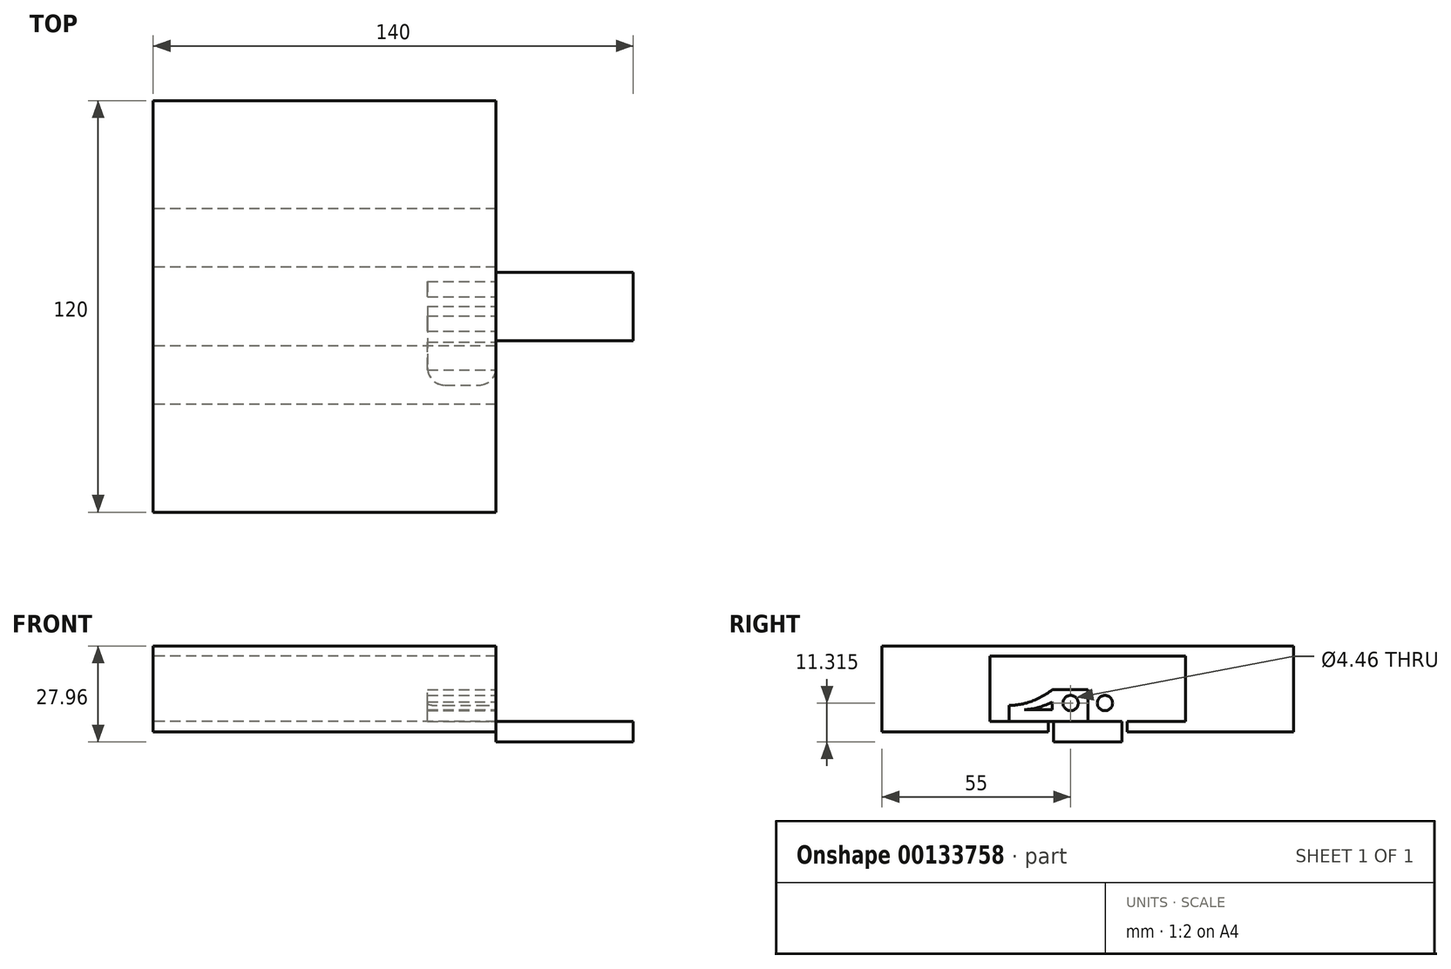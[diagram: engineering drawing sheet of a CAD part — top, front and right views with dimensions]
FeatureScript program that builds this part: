
annotation { "Feature Type Name" : "Feature", "Feature Type Description" : "" }
export const myFeature = defineFeature(function(context is Context, id is Id, definition is map)
    precondition{}
    {
        {
            var Q0;
            Q0=qCreatedBy(makeId("Right.planeOp"),FACE);
            var sketch = newSketch(context, id + "F0", { "sketchPlane" : qUnion([Q0])});
            skLineSegment(sketch, "E0", {"start": v(0, 0) * mm, "end": v(48.5, 0) * mm});
            skLineSegment(sketch, "E1", {"start": v(48.5, 0) * mm, "end": v(48.5, 25) * mm});
            skLineSegment(sketch, "E2", {"start": v(48.5, 25) * mm, "end": v(-71.5, 25) * mm});
            skLineSegment(sketch, "E3", {"start": v(-71.5, 25) * mm, "end": v(-71.5, 0) * mm});
            skLineSegment(sketch, "E4", {"start": v(-71.5, 0) * mm, "end": v(-23, 0) * mm});
            skLineSegment(sketch, "E5", {"start": v(-40, 0) * mm, "end": v(-40, 25) * mm});
            skLineSegment(sketch, "E6", {"start": v(17, 0) * mm, "end": v(17, 25) * mm});
            skLineSegment(sketch, "E7.0", {"start": v(-68.5, 3) * mm, "end": v(-23, 3) * mm});
            skLineSegment(sketch, "E7.1", {"start": v(0, 3) * mm, "end": v(45.5, 3) * mm});
            skLineSegment(sketch, "E7.2", {"start": v(45.5, 3) * mm, "end": v(45.5, 22) * mm});
            skLineSegment(sketch, "E7.3", {"start": v(45.5, 22) * mm, "end": v(-68.5, 22) * mm});
            skLineSegment(sketch, "E7.4", {"start": v(-68.5, 22) * mm, "end": v(-68.5, 3) * mm});
            skLineSegment(sketch, "E8", {"start": v(-23, 3) * mm, "end": v(-23, 0) * mm});
            skLineSegment(sketch, "E9", {"start": v(0, 3) * mm, "end": v(0, 0) * mm});
            skSolve(sketch);
        }
        {
            var Q0;
            {var subQ0=sQuery(id+"F0.wireOp",EDGE,"E8");Q0=makeQuery(id+"F0.imprint","IMPRINT",FACE,{"disambiguationData":[TD([[makeQuery(id+"F0.imprint","IMPRINT",EDGE,{"derivedFrom":subQ0}),-1.0]])]});}
            var Q1;
            {var subQ8=sQuery(id+"F0.wireOp",EDGE,"E3");Q1=makeQuery(id+"F0.imprint","IMPRINT",FACE,{"disambiguationData":[TD([[makeQuery(id+"F0.imprint","IMPRINT",EDGE,{"derivedFrom":subQ8}),1.0]])]});}
            var Q2;
            {var subQ0=sQuery(id+"F0.wireOp",EDGE,"E5");var subQ1=sQuery(id+"F0.wireOp",EDGE,"E2");var subQ2=makeQuery(id+"F0.imprint","INTERSECT",VERTEX,{"derivedFrom":[subQ1,subQ0]});Q2=makeQuery(id+"F0.imprint","IMPRINT",FACE,{"disambiguationData":[TD([[makeQuery(id+"F0.imprint","IMPRINT",EDGE,{"disambiguationData":[TD([[subQ2,1.0]])],"derivedFrom":subQ1}),1.0]])]});}
            var Q3;
            {var subQ6=sQuery(id+"F0.wireOp",EDGE,"E1");Q3=makeQuery(id+"F0.imprint","IMPRINT",FACE,{"disambiguationData":[TD([[makeQuery(id+"F0.imprint","IMPRINT",EDGE,{"derivedFrom":subQ6}),1.0]])]});}
            var Q4;
            {var subQ0=sQuery(id+"F0.wireOp",EDGE,"E9");Q4=makeQuery(id+"F0.imprint","IMPRINT",FACE,{"disambiguationData":[TD([[makeQuery(id+"F0.imprint","IMPRINT",EDGE,{"derivedFrom":subQ0}),1.0]])]});}
            var Q5;
            {var subQ5=sQuery(id+"F0.wireOp",EDGE,"E7.2");Q5=makeQuery(id+"F0.imprint","IMPRINT",FACE,{"disambiguationData":[TD([[makeQuery(id+"F0.imprint","IMPRINT",EDGE,{"derivedFrom":subQ5}),1.0]])]});}
            var Q6;
            {var subQ5=sQuery(id+"F0.wireOp",EDGE,"E7.4");Q6=makeQuery(id+"F0.imprint","IMPRINT",FACE,{"disambiguationData":[TD([[makeQuery(id+"F0.imprint","IMPRINT",EDGE,{"derivedFrom":subQ5}),1.0]])]});}
            extrude(context, id + "F1", {"entities" : qUnion([Q0, Q1, Q2, Q3, Q4, Q5, Q6]), "depth" : 100 * mm});
        }
        {
            var Q0;
            Q0=makeQuery(id+"F1.opExtrude","CAP_FACE",FACE,{"disambiguationData":[OSD([sQuery(id+"F0.wireOp",EDGE,"E0"),sQuery(id+"F0.wireOp",EDGE,"E1"),sQuery(id+"F0.wireOp",EDGE,"E2"),sQuery(id+"F0.wireOp",EDGE,"E3"),sQuery(id+"F0.wireOp",EDGE,"E4"),sQuery(id+"F0.wireOp",EDGE,"E5"),sQuery(id+"F0.wireOp",EDGE,"E6"),sQuery(id+"F0.wireOp",EDGE,"E7.0"),sQuery(id+"F0.wireOp",EDGE,"E7.1"),sQuery(id+"F0.wireOp",EDGE,"E7.3"),sQuery(id+"F0.wireOp",EDGE,"E8"),sQuery(id+"F0.wireOp",EDGE,"E9")])],"isStart":false});
            var sketch = newSketch(context, id + "F2", { "sketchPlane" : qUnion([Q0])});
            skLineSegment(sketch, "E10.bottom", {"start": v(-34.5, -2.96) * mm, "end": v(11.5, -2.96) * mm});
            skLineSegment(sketch, "E11", {"start": v(-11.5, 25) * mm, "end": v(-11.5, -62.96) * mm, "construction": true});
            skCircle(sketch, "E12", {"center": v(-16.5, 8.36) * mm, "radius": 2.23 * mm});
            skCircle(sketch, "E13.MirrorC", {"center": v(-6.5, 8.36) * mm, "radius": 2.23 * mm});
            skArc(sketch, "E14", {"start": v(-30.06, 6.4) * mm, "mid": v(-25.83, 7.13) * mm, "end": v(-21.84, 8.68) * mm});
            skLineSegment(sketch, "E15", {"start": v(-30.06, 6.4) * mm, "end": v(-21.84, 6.4) * mm});
            skLineSegment(sketch, "E16", {"start": v(-21.84, 6.4) * mm, "end": v(-21.84, 8.68) * mm});
            skLineSegment(sketch, "E17.MirrorCS", {"start": v(7.06, 6.4) * mm, "end": v(-1.16, 6.4) * mm});
            skLineSegment(sketch, "E18.MirrorCS", {"start": v(-1.16, 6.4) * mm, "end": v(-1.16, 8.68) * mm});
            skArc(sketch, "E19.MirrorCS", {"start": v(7.06, 6.4) * mm, "mid": v(2.83, 7.13) * mm, "end": v(-1.16, 8.68) * mm});
            skLineSegment(sketch, "E20.top", {"start": v(-21.5, -62.96) * mm, "end": v(-1.5, -62.96) * mm, "construction": true});
            skLineSegment(sketch, "E21.bottom", {"start": v(-34.5, -62.96) * mm, "end": v(11.5, -62.96) * mm});
            skLineSegment(sketch, "E21.left", {"start": v(-41.5, -55.96) * mm, "end": v(-41.5, -9.96) * mm});
            skLineSegment(sketch, "E21.right", {"start": v(18.5, -55.96) * mm, "end": v(18.5, -9.96) * mm});
            skPoint(sketch, "E22.orphan", {"position": v(-11.5, -18.14) * mm});
            skLineSegment(sketch, "E23.bottom", {"start": v(-21.5, -2.96) * mm, "end": v(-1.5, -2.96) * mm});
            skLineSegment(sketch, "E23.top", {"start": v(-21.5, -2.96) * mm, "end": v(-1.5, -2.96) * mm});
            skLineSegment(sketch, "E23.left", {"start": v(-21.5, -2.96) * mm, "end": v(-21.5, -2.96) * mm});
            skLineSegment(sketch, "E23.right", {"start": v(-1.5, -2.96) * mm, "end": v(-1.5, -2.96) * mm});
            skLineSegment(sketch, "E24.0", {"start": v(-28.5, -8.96) * mm, "end": v(5.5, -8.96) * mm});
            skLineSegment(sketch, "E24.1", {"start": v(-35.5, -49.96) * mm, "end": v(-35.5, -15.96) * mm});
            skLineSegment(sketch, "E24.2", {"start": v(-28.5, -56.96) * mm, "end": v(5.5, -56.96) * mm});
            skLineSegment(sketch, "E24.3", {"start": v(12.5, -49.96) * mm, "end": v(12.5, -15.96) * mm});
            skPoint(sketch, "E25.visualSharp", {"position": v(-41.5, -2.96) * mm});
            skArc(sketch, "E25.filletArc", {"start": v(-34.5, -2.96) * mm, "mid": v(-39.45, -5) * mm, "end": v(-41.5, -9.96) * mm});
            skPoint(sketch, "E26.visualSharp", {"position": v(18.5, -2.96) * mm});
            skArc(sketch, "E26.filletArc", {"start": v(18.5, -9.96) * mm, "mid": v(16.45, -5) * mm, "end": v(11.5, -2.96) * mm});
            skPoint(sketch, "E27.visualSharp", {"position": v(18.5, -62.96) * mm});
            skArc(sketch, "E27.filletArc", {"start": v(11.5, -62.96) * mm, "mid": v(16.45, -60.9) * mm, "end": v(18.5, -55.96) * mm});
            skPoint(sketch, "E28.visualSharp", {"position": v(-41.5, -62.96) * mm});
            skArc(sketch, "E28.filletArc", {"start": v(-41.5, -55.96) * mm, "mid": v(-39.45, -60.9) * mm, "end": v(-34.5, -62.96) * mm});
            skPoint(sketch, "E29.visualSharp", {"position": v(-35.5, -8.96) * mm});
            skArc(sketch, "E29.filletArc", {"start": v(-28.5, -8.96) * mm, "mid": v(-33.45, -11) * mm, "end": v(-35.5, -15.96) * mm});
            skPoint(sketch, "E30.visualSharp", {"position": v(12.5, -8.96) * mm});
            skArc(sketch, "E30.filletArc", {"start": v(12.5, -15.96) * mm, "mid": v(10.45, -11) * mm, "end": v(5.5, -8.96) * mm});
            skPoint(sketch, "E31.visualSharp", {"position": v(12.5, -56.96) * mm});
            skArc(sketch, "E31.filletArc", {"start": v(5.5, -56.96) * mm, "mid": v(10.45, -54.9) * mm, "end": v(12.5, -49.96) * mm});
            skPoint(sketch, "E32.visualSharp", {"position": v(-35.5, -56.96) * mm});
            skArc(sketch, "E32.filletArc", {"start": v(-35.5, -49.96) * mm, "mid": v(-33.45, -54.9) * mm, "end": v(-28.5, -56.96) * mm});
            skLineSegment(sketch, "E33.bottom", {"start": v(-35.5, -15.96) * mm, "end": v(-41.5, -15.96) * mm});
            skLineSegment(sketch, "E33.top", {"start": v(-35.5, -35.96) * mm, "end": v(-41.5, -35.96) * mm});
            skLineSegment(sketch, "E33.left", {"start": v(-35.5, -15.96) * mm, "end": v(-35.5, -35.96) * mm});
            skLineSegment(sketch, "E33.right", {"start": v(-41.5, -15.96) * mm, "end": v(-41.5, -35.96) * mm});
            skLineSegment(sketch, "E34.bottom", {"start": v(-11.5, 3.04) * mm, "end": v(-34.42, 3.04) * mm});
            skLineSegment(sketch, "E34.top", {"start": v(-11.5, 12.25) * mm, "end": v(-21.88, 12.25) * mm});
            skLineSegment(sketch, "E34.left", {"start": v(-11.5, 3.04) * mm, "end": v(-11.5, 12.25) * mm});
            skLineSegment(sketch, "E34.right", {"start": v(-34.42, 3.04) * mm, "end": v(-34.42, 7.65) * mm});
            skLineSegment(sketch, "E35.MirrorCS", {"start": v(-11.5, 12.25) * mm, "end": v(-1.12, 12.25) * mm});
            skLineSegment(sketch, "E36.MirrorCS", {"start": v(11.42, 3.04) * mm, "end": v(11.42, 7.65) * mm});
            skLineSegment(sketch, "E37.MirrorCS", {"start": v(-11.5, 3.04) * mm, "end": v(11.42, 3.04) * mm});
            skArc(sketch, "E38", {"start": v(-34.42, 7.65) * mm, "mid": v(-27.78, 8.93) * mm, "end": v(-21.88, 12.25) * mm});
            skArc(sketch, "E39.MirrorCS", {"start": v(11.42, 7.65) * mm, "mid": v(4.78, 8.93) * mm, "end": v(-1.12, 12.25) * mm});
            skPoint(sketch, "E40.orphan", {"position": v(-34.42, 12.25) * mm});
            skPoint(sketch, "E41.orphan", {"position": v(11.42, 12.25) * mm});
            skLineSegment(sketch, "E42.top", {"start": v(-21.5, 3.04) * mm, "end": v(-1.5, 3.04) * mm});
            skLineSegment(sketch, "E42.left", {"start": v(-21.5, -2.96) * mm, "end": v(-21.5, 3.04) * mm});
            skLineSegment(sketch, "E42.right", {"start": v(-1.5, -2.96) * mm, "end": v(-1.5, 3.04) * mm});
            skSolve(sketch);
        }
        {
            var Q0;
            Q0=makeQuery(id+"F2.imprint","IMPRINT",FACE,{"disambiguationData":[TD([[makeQuery(id+"F2.imprint","IMPRINT",EDGE,{"derivedFrom":sQuery(id+"F2.wireOp",EDGE,"E10.bottom")}),1.0]])]});
            extrude(context, id + "F3", {"entities" : qUnion([Q0]), "depth" : 40 * mm});
        }
        {
            var Q0;
            Q0=makeQuery(id+"F2.imprint","IMPRINT",FACE,{"disambiguationData":[TD([[makeQuery(id+"F2.imprint","IMPRINT",EDGE,{"derivedFrom":sQuery(id+"F2.wireOp",EDGE,"E12")}),-1.0]])]});
            var Q1;
            Q1=makeQuery(id+"F2.imprint","IMPRINT",FACE,{"disambiguationData":[TD([[makeQuery(id+"F2.imprint","IMPRINT",EDGE,{"derivedFrom":sQuery(id+"F2.wireOp",EDGE,"E13.MirrorC")}),1.0]])]});
            var Q2;
            Q2=makeQuery(id+"F2.imprint","IMPRINT",FACE,{"disambiguationData":[TD([[makeQuery(id+"F2.imprint","IMPRINT",EDGE,{"derivedFrom":sQuery(id+"F2.wireOp",EDGE,"E23.bottom")}),1.0]])]});
            var Q3;
            Q3=makeQuery(id+"F2.imprint","IMPRINT",FACE,{"disambiguationData":[TD([[makeQuery(id+"F2.imprint","IMPRINT",EDGE,{"derivedFrom":sQuery(id+"F2.wireOp",EDGE,"E21.bottom")}),1.0]])]});
            extrude(context, id + "F4", {"entities" : qUnion([Q0, Q1, Q2, Q3]), "oppositeDirection" : true, "depth" : 20 * mm});
        }
        {
            var Q0;
            Q0=makeQuery(id+"F4.opExtrude","CAP_EDGE",EDGE,{"disambiguationData":[OSD([sQuery(id+"F2.wireOp",EDGE,"E34.right")])],"isStart":true});
            var Q1;
            Q1=makeQuery(id+"F4.opExtrude","CAP_EDGE",EDGE,{"disambiguationData":[OSD([sQuery(id+"F2.wireOp",EDGE,"E36.MirrorCS")])],"isStart":true});
            var Q2;
            Q2=makeQuery(id+"F4.opExtrude","CAP_EDGE",EDGE,{"disambiguationData":[OSD([sQuery(id+"F2.wireOp",EDGE,"E42.right")])],"isStart":true});
            var Q3;
            Q3=makeQuery(id+"F4.opExtrude","CAP_EDGE",EDGE,{"disambiguationData":[OSD([sQuery(id+"F2.wireOp",EDGE,"E42.left")])],"isStart":true});
            var Q4;
            Q4=makeQuery(id+"F4.opExtrude","CAP_EDGE",EDGE,{"disambiguationData":[OSD([sQuery(id+"F2.wireOp",EDGE,"E42.left")])],"isStart":false});
            var Q5;
            Q5=makeQuery(id+"F4.opExtrude","CAP_EDGE",EDGE,{"disambiguationData":[OSD([sQuery(id+"F2.wireOp",EDGE,"E42.right")])],"isStart":false});
            var Q6;
            Q6=makeQuery(id+"F4.opExtrude","CAP_EDGE",EDGE,{"disambiguationData":[OSD([sQuery(id+"F2.wireOp",EDGE,"E34.right")])],"isStart":false});
            var Q7;
            Q7=makeQuery(id+"F4.opExtrude","CAP_EDGE",EDGE,{"disambiguationData":[OSD([sQuery(id+"F2.wireOp",EDGE,"E36.MirrorCS")])],"isStart":false});
            fillet(context, id + "F5", {"entities" : qUnion([Q0, Q1, Q2, Q3, Q4, Q5, Q6, Q7]), "radius" : 5 * mm, "tangentPropagation" : true, "allowEdgeOverflow" : false});
        }
        {
            var Q0;
            Q0=makeQuery(id+"F4.opExtrude","SWEPT_EDGE",EDGE,{"disambiguationData":[OSD([sQuery(id+"F2.wireOp",EDGE,"E21.left"),sQuery(id+"F2.wireOp",EDGE,"E33.bottom"),sQuery(id+"F2.wireOp",EDGE,"E33.right")])]});
            var Q1;
            Q1=makeQuery(id+"F4.opExtrude","SWEPT_EDGE",EDGE,{"disambiguationData":[OSD([sQuery(id+"F2.wireOp",EDGE,"E21.left"),sQuery(id+"F2.wireOp",EDGE,"E33.top"),sQuery(id+"F2.wireOp",EDGE,"E33.right")])]});
            fillet(context, id + "F6", {"entities" : qUnion([Q0, Q1]), "radius" : 5 * mm, "tangentPropagation" : true, "allowEdgeOverflow" : false});
        }
        {
            var Q0;
            Q0=makeQuery(id+"F4.opExtrude","SWEPT_EDGE",EDGE,{"disambiguationData":[OSD([sQuery(id+"F2.wireOp",EDGE,"E29.filletArc"),sQuery(id+"F2.wireOp",EDGE,"E33.bottom"),sQuery(id+"F2.wireOp",EDGE,"E33.left")])]});
            var Q1;
            Q1=makeQuery(id+"F4.opExtrude","SWEPT_EDGE",EDGE,{"disambiguationData":[OSD([sQuery(id+"F2.wireOp",EDGE,"E24.1"),sQuery(id+"F2.wireOp",EDGE,"E33.top"),sQuery(id+"F2.wireOp",EDGE,"E33.left")])]});
            chamfer(context, id + "F7", {"entities" : qUnion([Q0, Q1]), "width" : 2 * mm, "tangentPropagation" : true});
        }
        {
            var Q0;
            Q0=makeQuery(id+"F4.opExtrude","SWEPT_BODY",BODY,{"disambiguationData":[OSD([sQuery(id+"F2.wireOp",EDGE,"E12"),sQuery(id+"F2.wireOp",EDGE,"E13.MirrorC"),sQuery(id+"F2.wireOp",EDGE,"E14"),sQuery(id+"F2.wireOp",EDGE,"E15"),sQuery(id+"F2.wireOp",EDGE,"E16"),sQuery(id+"F2.wireOp",EDGE,"E17.MirrorCS"),sQuery(id+"F2.wireOp",EDGE,"E18.MirrorCS"),sQuery(id+"F2.wireOp",EDGE,"E19.MirrorCS"),sQuery(id+"F2.wireOp",EDGE,"E21.bottom"),sQuery(id+"F2.wireOp",EDGE,"E10.bottom"),sQuery(id+"F2.wireOp",EDGE,"E21.left"),sQuery(id+"F2.wireOp",EDGE,"E21.right"),sQuery(id+"F2.wireOp",EDGE,"E24.0"),sQuery(id+"F2.wireOp",EDGE,"E24.1"),sQuery(id+"F2.wireOp",EDGE,"E24.2"),sQuery(id+"F2.wireOp",EDGE,"E24.3"),sQuery(id+"F2.wireOp",EDGE,"E25.filletArc"),sQuery(id+"F2.wireOp",EDGE,"E26.filletArc"),sQuery(id+"F2.wireOp",EDGE,"E27.filletArc"),sQuery(id+"F2.wireOp",EDGE,"E28.filletArc"),sQuery(id+"F2.wireOp",EDGE,"E29.filletArc"),sQuery(id+"F2.wireOp",EDGE,"E30.filletArc"),sQuery(id+"F2.wireOp",EDGE,"E31.filletArc"),sQuery(id+"F2.wireOp",EDGE,"E32.filletArc"),sQuery(id+"F2.wireOp",EDGE,"E33.bottom"),sQuery(id+"F2.wireOp",EDGE,"E33.top"),sQuery(id+"F2.wireOp",EDGE,"E34.bottom"),sQuery(id+"F2.wireOp",EDGE,"E34.top"),sQuery(id+"F2.wireOp",EDGE,"E34.right"),sQuery(id+"F2.wireOp",EDGE,"E35.MirrorCS"),sQuery(id+"F2.wireOp",EDGE,"E36.MirrorCS"),sQuery(id+"F2.wireOp",EDGE,"E37.MirrorCS"),sQuery(id+"F2.wireOp",EDGE,"E38"),sQuery(id+"F2.wireOp",EDGE,"E39.MirrorCS"),sQuery(id+"F2.wireOp",EDGE,"E42.left"),sQuery(id+"F2.wireOp",EDGE,"E42.right")])]});
            deleteBodies(context, id + "F8", {"entities" : qUnion([Q0])});
        }
    });
